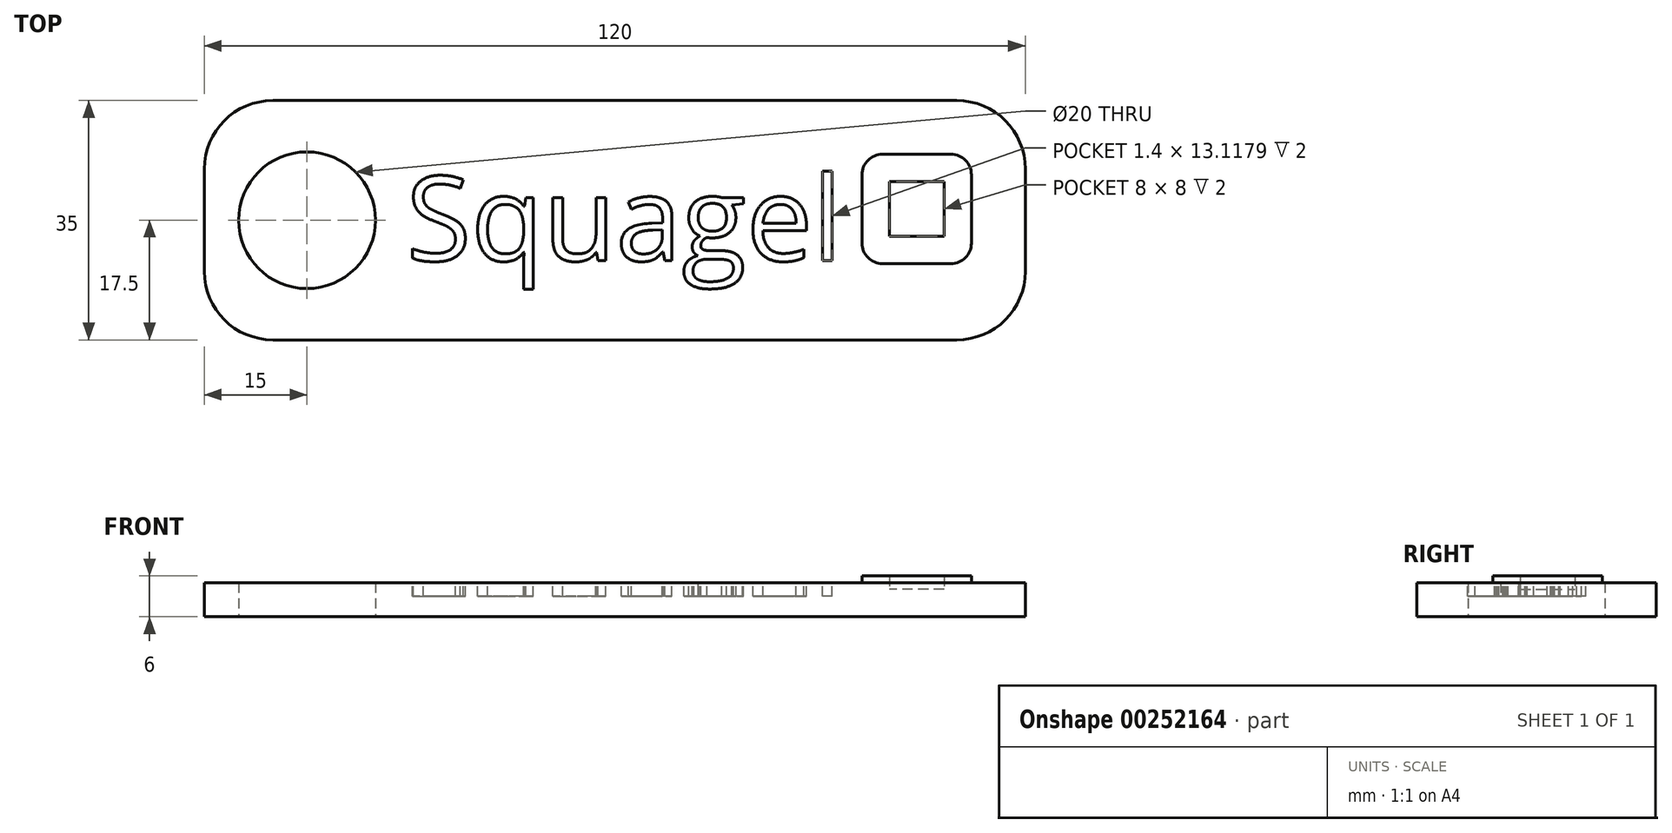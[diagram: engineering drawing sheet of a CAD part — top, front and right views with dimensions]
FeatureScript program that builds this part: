
annotation { "Feature Type Name" : "Feature", "Feature Type Description" : "" }
export const myFeature = defineFeature(function(context is Context, id is Id, definition is map)
    precondition{}
    {
        {
            var Q0;
            Q0=qCreatedBy(makeId("Top.planeOp"),FACE);
            var sketch = newSketch(context, id + "F0", { "sketchPlane" : qUnion([Q0])});
            skLineSegment(sketch, "E0.bottom", {"start": v(60, 17.5) * mm, "end": v(-60, 17.5) * mm});
            skLineSegment(sketch, "E0.top", {"start": v(60, -17.5) * mm, "end": v(-60, -17.5) * mm});
            skLineSegment(sketch, "E0.left", {"start": v(60, 17.5) * mm, "end": v(60, -17.5) * mm});
            skLineSegment(sketch, "E0.right", {"start": v(-60, 17.5) * mm, "end": v(-60, -17.5) * mm});
            skPoint(sketch, "E0.middle", {"position": v(0, 0) * mm});
            skCircle(sketch, "E1", {"center": v(-45, 0) * mm, "radius": 10 * mm});
            skSolve(sketch);
        }
        {
            var Q0;
            Q0=makeQuery(id+"F0.imprint","IMPRINT",FACE,{"disambiguationData":[TD([[makeQuery(id+"F0.imprint","IMPRINT",EDGE,{"derivedFrom":sQuery(id+"F0.wireOp",EDGE,"E0.bottom")}),1.0]])]});
            extrude(context, id + "F1", {"entities" : qUnion([Q0]), "depth" : 5 * mm});
        }
        {
            var Q0;
            Q0=makeQuery(id+"F1.opExtrude","SWEPT_EDGE",EDGE,{"disambiguationData":[OSD([sQuery(id+"F0.wireOp",EDGE,"E0.top"),sQuery(id+"F0.wireOp",EDGE,"E0.right")])]});
            var Q1;
            Q1=makeQuery(id+"F1.opExtrude","SWEPT_EDGE",EDGE,{"disambiguationData":[OSD([sQuery(id+"F0.wireOp",EDGE,"E0.bottom"),sQuery(id+"F0.wireOp",EDGE,"E0.right")])]});
            var Q2;
            Q2=makeQuery(id+"F1.opExtrude","SWEPT_EDGE",EDGE,{"disambiguationData":[OSD([sQuery(id+"F0.wireOp",EDGE,"E0.top"),sQuery(id+"F0.wireOp",EDGE,"E0.left")])]});
            var Q3;
            Q3=makeQuery(id+"F1.opExtrude","SWEPT_EDGE",EDGE,{"disambiguationData":[OSD([sQuery(id+"F0.wireOp",EDGE,"E0.bottom"),sQuery(id+"F0.wireOp",EDGE,"E0.left")])]});
            fillet(context, id + "F2", {"entities" : qUnion([Q0, Q1, Q2, Q3]), "radius" : 10 * mm, "tangentPropagation" : true, "allowEdgeOverflow" : false});
        }
        {
            var Q0;
            Q0=makeQuery(id+"F1.opExtrude","CAP_FACE",FACE,{"disambiguationData":[OSD([sQuery(id+"F0.wireOp",EDGE,"E0.bottom"),sQuery(id+"F0.wireOp",EDGE,"E0.top"),sQuery(id+"F0.wireOp",EDGE,"E0.left"),sQuery(id+"F0.wireOp",EDGE,"E0.right"),sQuery(id+"F0.wireOp",EDGE,"E1")])],"isStart":false});
            var sketch = newSketch(context, id + "F3", { "sketchPlane" : qUnion([Q0])});
            skText(sketch, "E2", { "text": "Squagel", "fontName": "OpenSans-Regular.ttf"});
            const initialGuessF3  = {"E2": [-0.0305, -0.00592, 1, 0, 0.01243]};
            skSetInitialGuess(sketch, initialGuessF3);
            skSolve(sketch);
        }
        {
            var Q0;
            Q0 = qSketchRegion(id + "F3", true);
            extrude(context, id + "F4", {"entities" : qUnion([Q0]), "operationType" : NewBodyOperationType.REMOVE, "oppositeDirection" : true, "depth" : 2 * mm});
        }
        {
            var Q0;
            {var subQ0=sQuery(id+"F0.wireOp",EDGE,"E0.left");var subQ1=sQuery(id+"F0.wireOp",EDGE,"E0.bottom");var subQ2=sQuery(id+"F0.wireOp",EDGE,"E0.right");var subQ3=sQuery(id+"F0.wireOp",EDGE,"E0.top");var subQ4=sQuery(id+"F0.wireOp",EDGE,"E1");Q0=makeQuery(id+"F4.boolean.opBoolean","SPLIT",FACE,{"disambiguationData":[TD([makeQuery(id+"F1.opExtrude","SWEPT_FACE",FACE,{"disambiguationData":[OSD([subQ1])]})])],"derivedFrom":makeQuery(id+"F1.opExtrude","CAP_FACE",FACE,{"disambiguationData":[OSD([subQ1,subQ3,subQ0,subQ2,subQ4])],"isStart":false})});}
            var sketch = newSketch(context, id + "F5", { "sketchPlane" : qUnion([Q0])});
            skLineSegment(sketch, "E3.bottom", {"start": v(52.12, -6.36) * mm, "end": v(36.12, -6.36) * mm});
            skLineSegment(sketch, "E3.top", {"start": v(52.12, 9.64) * mm, "end": v(36.12, 9.64) * mm});
            skLineSegment(sketch, "E3.left", {"start": v(52.12, -6.36) * mm, "end": v(52.12, 9.64) * mm});
            skLineSegment(sketch, "E3.right", {"start": v(36.12, -6.36) * mm, "end": v(36.12, 9.64) * mm});
            skPoint(sketch, "E3.middle", {"position": v(44.12, 1.64) * mm});
            skLineSegment(sketch, "E4.bottom", {"start": v(48.12, -2.36) * mm, "end": v(40.12, -2.36) * mm});
            skLineSegment(sketch, "E4.top", {"start": v(48.12, 5.64) * mm, "end": v(40.12, 5.64) * mm});
            skLineSegment(sketch, "E4.left", {"start": v(48.12, -2.36) * mm, "end": v(48.12, 5.64) * mm});
            skLineSegment(sketch, "E4.right", {"start": v(40.12, -2.36) * mm, "end": v(40.12, 5.64) * mm});
            skSolve(sketch);
        }
        {
            var Q0;
            Q0=makeQuery(id+"F5.imprint","IMPRINT",FACE,{"disambiguationData":[TD([[makeQuery(id+"F5.imprint","IMPRINT",EDGE,{"derivedFrom":sQuery(id+"F5.wireOp",EDGE,"E3.bottom")}),-1.0]])]});
            extrude(context, id + "F6", {"entities" : qUnion([Q0]), "operationType" : NewBodyOperationType.ADD, "depth" : 1 * mm});
        }
        {
            var Q0;
            {var subQ0=sQuery(id+"F0.wireOp",EDGE,"E0.left");var subQ1=sQuery(id+"F0.wireOp",EDGE,"E0.bottom");var subQ2=sQuery(id+"F0.wireOp",EDGE,"E0.right");var subQ3=sQuery(id+"F0.wireOp",EDGE,"E0.top");var subQ4=sQuery(id+"F0.wireOp",EDGE,"E1");Q0=makeQuery(id+"F6.boolean.opBoolean","SPLIT",FACE,{"disambiguationData":[TD([makeQuery(id+"F6.opExtrude","SWEPT_FACE",FACE,{"disambiguationData":[OSD([sQuery(id+"F5.wireOp",EDGE,"E4.bottom")])]})])],"derivedFrom":makeQuery(id+"F4.boolean.opBoolean","SPLIT",FACE,{"disambiguationData":[TD([makeQuery(id+"F1.opExtrude","SWEPT_FACE",FACE,{"disambiguationData":[OSD([subQ1])]})])],"derivedFrom":makeQuery(id+"F1.opExtrude","CAP_FACE",FACE,{"disambiguationData":[OSD([subQ1,subQ3,subQ0,subQ2,subQ4])],"isStart":false})})});}
            extrude(context, id + "F7", {"entities" : qUnion([Q0]), "operationType" : NewBodyOperationType.REMOVE, "oppositeDirection" : true, "depth" : 1 * mm});
        }
        {
            var Q0;
            Q0=makeQuery(id+"F6.opExtrude","SWEPT_EDGE",EDGE,{"disambiguationData":[OSD([sQuery(id+"F5.wireOp",EDGE,"E3.bottom"),sQuery(id+"F5.wireOp",EDGE,"E3.left")])]});
            var Q1;
            Q1=makeQuery(id+"F6.opExtrude","SWEPT_EDGE",EDGE,{"disambiguationData":[OSD([sQuery(id+"F5.wireOp",EDGE,"E3.bottom"),sQuery(id+"F5.wireOp",EDGE,"E3.right")])]});
            var Q2;
            Q2=makeQuery(id+"F6.opExtrude","SWEPT_EDGE",EDGE,{"disambiguationData":[OSD([sQuery(id+"F5.wireOp",EDGE,"E3.top"),sQuery(id+"F5.wireOp",EDGE,"E3.right")])]});
            var Q3;
            Q3=makeQuery(id+"F6.opExtrude","SWEPT_EDGE",EDGE,{"disambiguationData":[OSD([sQuery(id+"F5.wireOp",EDGE,"E3.top"),sQuery(id+"F5.wireOp",EDGE,"E3.left")])]});
            fillet(context, id + "F8", {"entities" : qUnion([Q0, Q1, Q2, Q3]), "radius" : 3 * mm, "tangentPropagation" : true, "allowEdgeOverflow" : false});
        }
    });
